# Revit family: Save-Up-Standaard
name_source: partatom
category: Security Devices
revit_build: Autodesk Revit Architecture 2012 (Build: 20110309_2315(x64)
units: mm (PartAtom-declared; Revit-internal decimal feet)

## types (4) — shared parameters
Description = Save-Up fall protection system
End-void = 12 mm  [stored 0.0393701 ft]
Manufacturer = A&T Save Up BV
Material = Steel, PP and TPE
Model = Safe Up Roof System
Start-void = 10 mm  [stored 0.0328084 ft]
URL = http://www.save-up.nl
Universele onderpan = 1x

## per-type parameters (varying)
| type | Grote drukverdeelplaat | Kleine drukverdeelplaat | Opvulring |
| Houten dakbeschot |  | 2x | 4x |
| Enkelschalig dakelement | 1x | 1x |  |
| Dubbelschalig dakelement |  | 2x |  |
| Sandwich dakelement | 2x | 1x | 1x |

note: [stored X ft] marks values corroborated as IEEE doubles in the binary element streams (Revit-internal decimal feet)

## geometry (parser evidence)
native form markers: Sweep x1
no freeform markers — native parametric forms only
